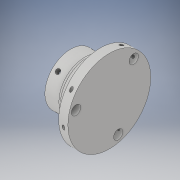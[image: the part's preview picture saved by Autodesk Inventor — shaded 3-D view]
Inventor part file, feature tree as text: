
AUTODESK INVENTOR PART (.ipt)
format: ipt  version: 2019 (Build 230136000, 136)  size: 381,440 bytes
history: native  units: in
note: dims shown in document units (in); Inventor stores cm internally (conversion verified against a paired STEP export)
features: sketch x21, extrude x10, plane x8, mirror x4, projected_geometry x4, pattern_circular x2, thread x2, fillet x2, revolve x1, sweep x1
ambient origin geometry x8: Origin, YZ Plane, XZ Plane, XY Plane, X Axis, Y Axis, Z Axis, Center Point
bodies: Solid1 (feature_tree), Solid2 (feature_tree)
feature tree (55):
  extrude  "Extrusion1"  Depth=1.7323in
  extrude  "Extrusion3"  Depth=1.2402in
  extrude  "Extrusion4"  Depth=1.1811in TaperAngle=0.0deg
  pattern_circular  "Circular Pattern1"  Count=4 Angle=360.0deg
  sketch  "Sketch6"  dims[d16=0.3937in d17=45.0deg]
  plane  "Work Plane1"
  extrude  "Extrusion5"  TaperAngle=45.0deg  [1 undecoded]
  plane  "Work Plane2"
  mirror  "Mirror1"
  extrude  "Extrusion6"  TaperAngle=45.0deg  [1 undecoded]
  extrude  "Extrusion7"  Depth=0.2362in TaperAngle=0.0deg
  sketch  "Sketch11"  dims[d26=0.3937in d27=0.0in d28=0.0118in]
  plane  "Work Plane3"
  extrude  "Extrusion8"  TaperAngle=45.0deg  [1 undecoded]
  thread  "Thread1"  [1 undecoded]
  mirror  "Mirror2"
  extrude  "Extrusion9"  Depth=0.3937in
  revolve  "Revolution1"  [1 undecoded]
  mirror  "Mirror3"
  fillet  "Fillet1"  Radius=0.4724in
  fillet  "Fillet2"  Radius=0.0098in
  extrude  "Extrusion10"  Depth=0.4724in
  extrude  "Extrusion11"  Depth=0.3937in TaperAngle=0.0deg
  sketch  "Sketch18"  dims[d46=1.7717in]
  plane  "Work Plane4"
  sketch  "Sketch19"  dims[d47=90.0deg]
  plane  "Work Plane5"
  sketch  "Sketch22"  dims[d48=90.0deg]
  plane  "Work Plane6"
  sketch  "Sketch23"  dims[d49=0.1575in]
  sweep  "Sweep1"
  plane  "Work Plane7"
  thread  "Thread3"  [1 undecoded]
  sketch  "Sketch25"  dims[d51=0.3937in d52=0.0in]
  sketch  "Sketch26"  dims[d53=1.4764in]
  sketch  "Sketch27"  dims[d54=45.0deg d55=0.3976in d56=0.3937in d57=0.0in d58=45.0deg d59=0.1969in d60=180.0deg d64=1.1811in d65=360.0deg d69=1.5748in d70=120.0deg d71=0.1181in d72=0.0in d73=0.0in d74=-1.5748in d75=0.3937in d76=0.0in d78=1.5748in d79=30.0deg d82=135.0deg]
  plane  "Work Plane10"
  mirror  "Mirror4"
  pattern_circular  "Circular Pattern2"  [2 undecoded]
  sketch  "Sketch2"  dims[d3=0.7874in d4=1.7323in]
  sketch  "Sketch4"  dims[d5=0.4724in d6=0.0in d9=1.2402in]
  sketch  "Sketch5"  dims[d10=0.2008in d11=1.1811in d12=0.0in d13=1.5748in d14=360.0deg]
  sketch  "Sketch7"  dims[d18=0.1181in d19=45.0deg]
  sketch  "Sketch8"  dims[d20=0.3543in d21=0.2362in d22=0.0in]
  projected_geometry  "Projected Loop1"
  sketch  "Sketch9"  dims[d23=0.8661in d24=45.0deg d25=0.2047in]
  sketch  "Sketch12"  dims[d29=0.4724in d30=0.0in d31=0.2362in d32=0.4724in d33=0.0in d34=0.0098in]
  sketch  "Sketch13"  dims[d35=45.0deg d36=0.4724in]
  sketch  "Sketch14"  dims[d37=0.1969in d38=0.3937in d39=0.0in]
  sketch  "Sketch15"  dims[d40=0.3937in d41=0.0in d42=0.1969in d43=0.0in d44=0.5906in]
  projected_geometry  "Projected Loop2"
  sketch  "Sketch17"  dims[d45=180.0deg]
  projected_geometry  "Projected Loop3"
  sketch  "Sketch24"  dims[d50=0.0157in]
  projected_geometry  "Projected Loop4"
note: 8 required parameter values undecoded (feature->parameter linkage not recoverable at this tier; creation-order binding heuristic only, values carry confidence <= 0.55)